# Revit family: IS_Prosys_R0153_BIM_DE
name_source: partatom
category: Plumbing Fixtures
revit_build: Autodesk Revit 2017 (Build: 20160225_1515(x64)
units: mm (PartAtom-declared; Revit-internal decimal feet)

## family parameters
Cut with Voids When Loaded = No
Host = Face
OmniClass Number = 23.45.05.21.11.11
OmniClass Title = Water Operated Water Closets
Part Type = Normal
Room Calculation Point = No
Round Connector Dimension = Use Diameter
Shared = Yes

## types (2) — shared parameters
Accessories = https://www.idealstandardnederland.nl
AreaUnits = millimeters
Assembly Code = C1030200
AssetType = Fixed
BREEAMApproved = No
Brand = Ideal Standard Netherlands
ConnectionType = Plumbing
CurrencyUnit = €
DurationUnit = year
ECA = No
ExpectedLife = 30
Finish = White
Help = https://www.idealstandardnederland.nl
IfcExportAs = IfcSanitaryTerminalType
IfcExportType = CISTERN
InstallationInstructions = https://www.idealstandardnederland.nl
LinearUnits = millimeters
Manufacturer = https://www.idealstandardnederland.nl
ManufacturerURL = https://www.idealstandardnederland.nl
NBSDescription = WC cistern fittings
NBSReference = 45-30-70/387
NettWeight = 12.20 Kg
NominalDepth = 140 mm
NominalLength = 140 mm
ProductInformation = https://www.idealstandardnederland.nl
Shape = Sculptured
Space = Internal
ToiletPanType = WashDown
ToiletType = Other
URL = https://www.idealstandardnederland.nl
Uniclass2 = Pr_40_20_93_89
Uniclass2015Code = Pr_40_20_93
Uniclass2015Description = Urinal and WC fittings
Uniclass2015Reference = Pr_40_20_93
Uniclass2015Title = Urinal and WC fittings
Uniclass2015Version = v1.1
Version = 1
VolumeUnits = Litres
WRAS = No
WarrantyDescription = Manufacturers Warranty
WarrantyDurationParts = 0
WarrantyDurationUnit = year
WarrantyGuarantorParts = https://www.idealstandardnederland.nl
WaterEfficientProduct = No
zero-valued in all types: CWFU, Cost, Default Elevation, HWFU, SpilloverLevel, WFU

## per-type parameters (varying)
| type | BIMObjectName | BarCode | Description | Features | Model | ModelNumber | ModelReference | Name | NominalHeight | NominalWidth | Size |
| R009467 - PROSYS WC FRAME 120 M CL1 | IS_IdealStandard_UrinalandWCfittings_Prosys_R0094 | 3391500579538 | PROSYS FRAME 1100 DRY WC 120 CL1 | FRAME 1100 DRY WC 120 CL1 | R0094 | R0094 | PROSYS FRAME 1100 DRY WC 120 CL1 | UrinalandWCfittings_Prosys_R0094_IdealStandard | 530 mm | 500 mm  [stored 1.64042 ft] | 530 x 140 x 500 mm |
| R015367 - PROSYS WC FRAME 120 M CL2 | IS_IdealStandard_UrinalandWCfittings_Prosys_R0153 | 3391500580862 | PROSYS FRAME 1100 WC 120 M CL2 | FRAME 1100 WC 120 M CL2 | R0153 | R0153 | PROSYS FRAME 1100 WC 120 M CL2 | UrinalandWCfittings_Prosys_R0153_IdealStandard | 1134 mm  [stored 3.72047 ft] | 1180 mm | 1134 x 140 x 1180 mm |

note: [stored X ft] marks values corroborated as IEEE doubles in the binary element streams (Revit-internal decimal feet)

## geometry (parser evidence)
native form markers: Sweep x5
no freeform markers — native parametric forms only
